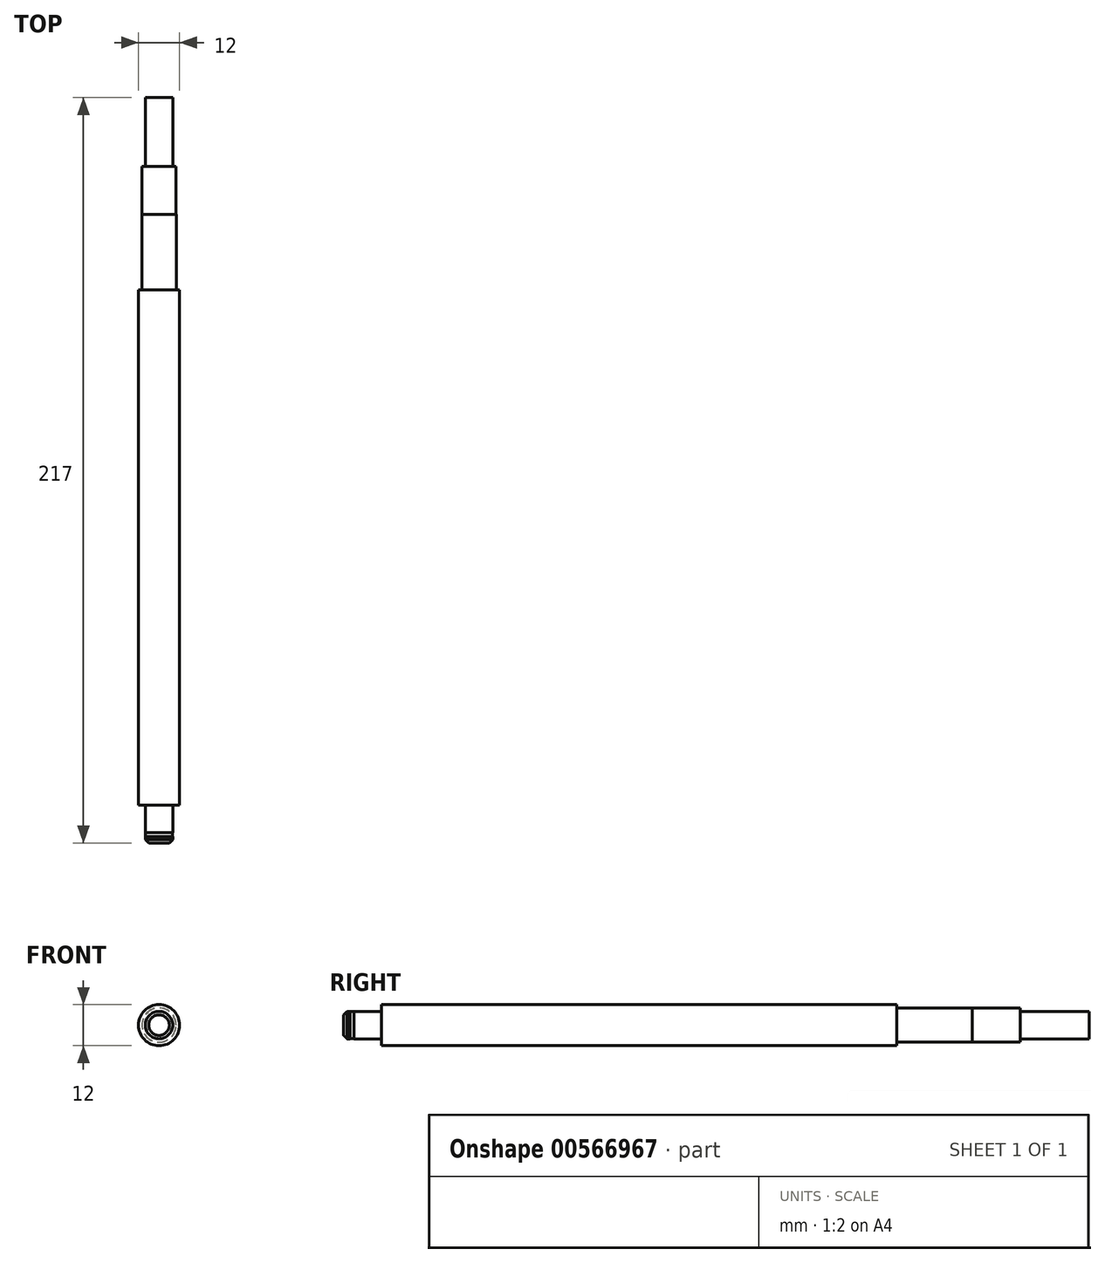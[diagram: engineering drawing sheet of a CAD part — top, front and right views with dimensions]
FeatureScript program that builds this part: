
annotation { "Feature Type Name" : "Feature", "Feature Type Description" : "" }
export const myFeature = defineFeature(function(context is Context, id is Id, definition is map)
    precondition{}
    {
        {
            var Q0;
            Q0=qCreatedBy(makeId("Front.planeOp"),FACE);
            var sketch = newSketch(context, id + "F0", { "sketchPlane" : qUnion([Q0])});
            skCircle(sketch, "E0", {"center": v(0, 0) * mm, "radius": 6 * mm});
            skSolve(sketch);
        }
        {
            var Q0;
            Q0=makeQuery(id+"F0.imprint","IMPRINT",FACE,{"disambiguationData":[TD([[makeQuery(id+"F0.imprint","IMPRINT",EDGE,{"derivedFrom":sQuery(id+"F0.wireOp",EDGE,"E0")}),1.0]])]});
            extrude(context, id + "F1", {"entities" : qUnion([Q0]), "depth" : 150 * mm});
        }
        {
            var Q0;
            Q0=makeQuery(id+"F1.opExtrude","CAP_FACE",FACE,{"disambiguationData":[OSD([sQuery(id+"F0.wireOp",EDGE,"E0")])],"isStart":true});
            var sketch = newSketch(context, id + "F2", { "sketchPlane" : qUnion([Q0])});
            skCircle(sketch, "E1", {"center": v(0, 0) * mm, "radius": 5 * mm});
            skSolve(sketch);
        }
        {
            var Q0;
            Q0=makeQuery(id+"F2.imprint","IMPRINT",FACE,{"disambiguationData":[TD([[makeQuery(id+"F2.imprint","IMPRINT",EDGE,{"derivedFrom":sQuery(id+"F2.wireOp",EDGE,"E1")}),1.0]])]});
            extrude(context, id + "F3", {"entities" : qUnion([Q0]), "operationType" : NewBodyOperationType.ADD, "depth" : 22 * mm});
        }
        {
            var Q0;
            Q0=makeQuery(id+"F3.opExtrude","CAP_FACE",FACE,{"disambiguationData":[OSD([sQuery(id+"F2.wireOp",EDGE,"E1")])],"isStart":false});
            var sketch = newSketch(context, id + "F4", { "sketchPlane" : qUnion([Q0])});
            skCircle(sketch, "E2", {"center": v(0, 0) * mm, "radius": 4.95 * mm});
            skSolve(sketch);
        }
        {
            var Q0;
            Q0=qSketchRegion(id+"F4",true);
            extrude(context, id + "F5", {"entities" : qUnion([Q0]), "operationType" : NewBodyOperationType.ADD, "depth" : 14 * mm});
        }
        {
            var Q0;
            Q0=makeQuery(id+"F5.opExtrude","CAP_FACE",FACE,{"disambiguationData":[OSD([sQuery(id+"F4.wireOp",EDGE,"E2")])],"isStart":false});
            var sketch = newSketch(context, id + "F6", { "sketchPlane" : qUnion([Q0])});
            skCircle(sketch, "E3", {"center": v(0, 0) * mm, "radius": 4 * mm});
            skSolve(sketch);
        }
        {
            var Q0;
            Q0=makeQuery(id+"F6.imprint","IMPRINT",FACE,{"disambiguationData":[TD([[makeQuery(id+"F6.imprint","IMPRINT",EDGE,{"derivedFrom":sQuery(id+"F6.wireOp",EDGE,"E3")}),1.0]])]});
            extrude(context, id + "F7", {"entities" : qUnion([Q0]), "operationType" : NewBodyOperationType.ADD, "depth" : 20 * mm});
        }
        {
            var Q0;
            Q0=makeQuery(id+"F1.opExtrude","CAP_FACE",FACE,{"disambiguationData":[OSD([sQuery(id+"F0.wireOp",EDGE,"E0")])],"isStart":false});
            var sketch = newSketch(context, id + "F8", { "sketchPlane" : qUnion([Q0])});
            skCircle(sketch, "E4", {"center": v(0, 0) * mm, "radius": 4 * mm});
            skSolve(sketch);
        }
        {
            var Q0;
            Q0=makeQuery(id+"F8.imprint","IMPRINT",FACE,{"disambiguationData":[TD([[makeQuery(id+"F8.imprint","IMPRINT",EDGE,{"derivedFrom":sQuery(id+"F8.wireOp",EDGE,"E4")}),1.0]])]});
            extrude(context, id + "F9", {"entities" : qUnion([Q0]), "operationType" : NewBodyOperationType.ADD, "depth" : 8 * mm});
        }
        {
            var Q0;
            Q0=makeQuery(id+"F9.opExtrude","CAP_FACE",FACE,{"disambiguationData":[OSD([sQuery(id+"F8.wireOp",EDGE,"E4")])],"isStart":false});
            var sketch = newSketch(context, id + "F10", { "sketchPlane" : qUnion([Q0])});
            skCircle(sketch, "E5", {"center": v(0, 0) * mm, "radius": 3.9 * mm});
            skSolve(sketch);
        }
        {
            var Q0;
            Q0=makeQuery(id+"F10.imprint","IMPRINT",FACE,{"disambiguationData":[TD([[makeQuery(id+"F10.imprint","IMPRINT",EDGE,{"derivedFrom":sQuery(id+"F10.wireOp",EDGE,"E5")}),1.0]])]});
            extrude(context, id + "F11", {"entities" : qUnion([Q0]), "operationType" : NewBodyOperationType.ADD, "depth" : 1.15 * mm});
        }
        {
            var Q0;
            Q0=makeQuery(id+"F11.opExtrude","CAP_FACE",FACE,{"disambiguationData":[OSD([sQuery(id+"F10.wireOp",EDGE,"E5")])],"isStart":false});
            var sketch = newSketch(context, id + "F12", { "sketchPlane" : qUnion([Q0])});
            skCircle(sketch, "E6", {"center": v(0, 0) * mm, "radius": 4 * mm});
            skSolve(sketch);
        }
        {
            var Q0;
            Q0=qSketchRegion(id+"F12",true);
            extrude(context, id + "F13", {"entities" : qUnion([Q0]), "operationType" : NewBodyOperationType.ADD, "depth" : 1.85 * mm});
        }
        {
            var Q0;
            Q0=makeQuery(id+"F13.opExtrude","CAP_EDGE",EDGE,{"disambiguationData":[OSD([sQuery(id+"F12.wireOp",EDGE,"E6")])],"isStart":false});
            chamfer(context, id + "F14", {"entities" : qUnion([Q0]), "width" : 1 * mm, "tangentPropagation" : true});
        }
    });
